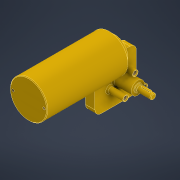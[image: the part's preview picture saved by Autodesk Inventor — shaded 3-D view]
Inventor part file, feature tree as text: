
AUTODESK INVENTOR PART (.ipt)
format: ipt  version: 2021 (Build 250183000, 183)  size: 283,648 bytes
history: native  units: mm
features: sketch x9, extrude x6, plane x5, chamfer x5, thread x3, projected_geometry x2, revolve x1, fillet x1, hole x1
ambient origin geometry x8: Origin, YZ Plane, XZ Plane, XY Plane, X Axis, Y Axis, Z Axis, Center Point
bodies: Solid1 (feature_tree)
feature tree (33):
  extrude  "Extrusion1"  Depth=139.0mm TaperAngle=0.0deg
  plane  "Work Plane1"
  plane  "Work Plane2"
  sketch  "Sketch2"  dims[d3=62.0mm d4=0.0mm]
  plane  "Work Plane3"
  sketch  "Sketch3"  dims[d5=0.0mm d6=62.0mm]
  extrude  "Extrusion2"  TaperAngle=0.0deg  [1 undecoded]
  revolve  "Revolution1"  [1 undecoded]
  plane  "Work Plane4"
  extrude  "Extrusion3"  Depth=15.0mm TaperAngle=0.0deg
  extrude  "Extrusion4"  Depth=99.5mm
  chamfer  "Chamfer1"  Distance=1.0mm
  fillet  "Fillet1"  Radius=2.0mm
  hole  "Hole1"  [1 undecoded]
  chamfer  "Chamfer3"  Distance=1.0mm
  chamfer  "Chamfer4"  Distance=4.0mm
  plane  "Work Plane5"
  extrude  "Extrusion5"  TaperAngle=0.0deg  [1 undecoded]
  chamfer  "Chamfer5"  Angle=90.0deg  [1 undecoded]
  extrude  "Extrusion6"  Depth=3.0mm
  thread  "Thread1"  [1 undecoded]
  thread  "Thread2"  [1 undecoded]
  thread  "Thread3"  [1 undecoded]
  chamfer  "Chamfer6"  Distance=30.0mm
  sketch  "Sketch1"  dims[d0=60.0mm d1=139.0mm d2=0.0mm]
  sketch  "Sketch4"  dims[d7=34.6mm d8=15.0mm d9=0.0mm]
  sketch  "Sketch5"  dims[d11=0.0mm d12=99.5mm]
  sketch  "Sketch6"  dims[d13=66.5mm]
  projected_geometry  "Projected Loop1"
  sketch  "Sketch7"  dims[d14=100.6mm]
  sketch  "Sketch8"  dims[d15=4.5mm]
  projected_geometry  "Projected Loop2"
  sketch  "Sketch9"  dims[d16=22.0mm d17=1.0mm d18=2.0mm d19=1.0mm d20=1.0mm d21=4.0mm d22=0.0mm d23=90.0deg d28=3.0mm d29=0.0mm d30=13.0mm d31=4.5mm d32=30.0mm d33=0.0mm d34=1.3mm d35=0.0mm d36=1.0mm d37=2.0mm d38=45.0deg d39=10.0mm d42=0.0mm d43=0.0mm d44=25.0mm d45=25.0mm d46=4.134mm d47=8.0mm d48=4.0mm d49=2.0mm d50=90.0deg d51=8.0mm d52=20.594885mm d56=9.0mm d57=2.0mm d58=45.0deg d59=1.0mm d60=2.0mm d61=45.0deg d62=-4.0mm d64=36.0mm d67=120.0deg d68=120.0deg d69=6.0mm d70=9.0mm d71=6.0mm d72=9.0mm d73=6.0mm d74=9.0mm d75=10.0mm d76=0.0mm d77=2.0mm d78=2.0mm d79=45.0deg d80=6.0mm d81=10.0mm d82=0.0mm d83=25.5mm d84=0.0mm d85=25.5mm d86=0.0mm d87=25.5mm d88=0.0mm d89=1.0mm d90=2.0mm d91=45.0deg]
note: 8 required parameter values undecoded (feature->parameter linkage not recoverable at this tier; creation-order binding heuristic only, values carry confidence <= 0.55)